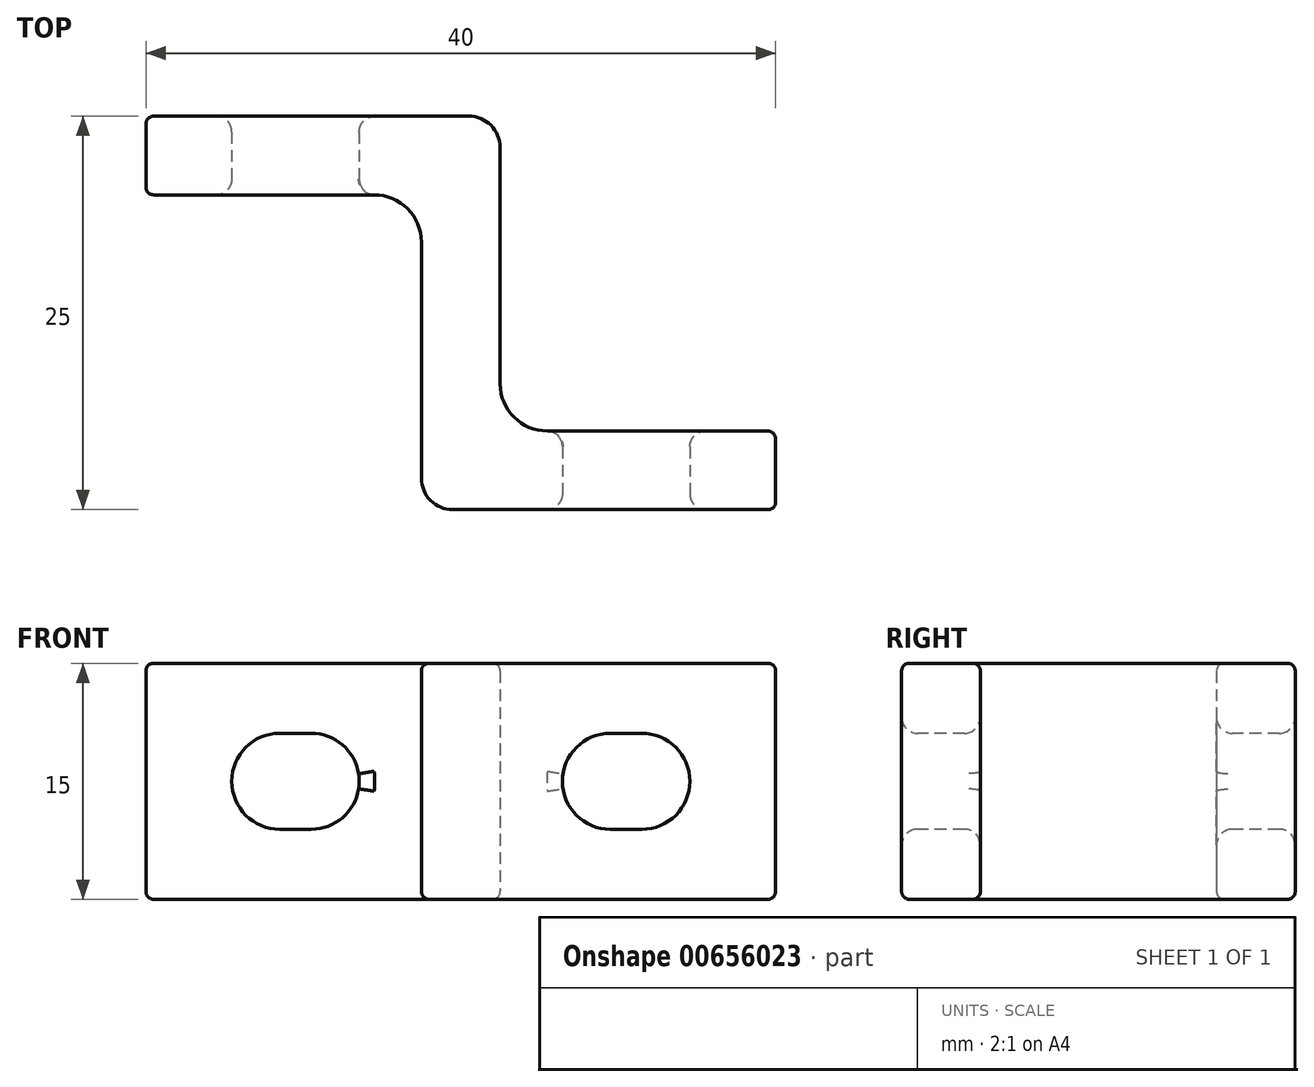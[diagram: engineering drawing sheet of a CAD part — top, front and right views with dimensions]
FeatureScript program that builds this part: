
annotation { "Feature Type Name" : "Feature", "Feature Type Description" : "" }
export const myFeature = defineFeature(function(context is Context, id is Id, definition is map)
    precondition{}
    {
        {
            var Q0;
            Q0=qCreatedBy(makeId("Top.planeOp"),FACE);
            var sketch = newSketch(context, id + "F0", { "sketchPlane" : qUnion([Q0])});
            skLineSegment(sketch, "E0", {"start": v(0, 0) * mm, "end": v(22.5, 0) * mm});
            skLineSegment(sketch, "E1", {"start": v(22.5, 0) * mm, "end": v(22.5, -20) * mm});
            skLineSegment(sketch, "E2", {"start": v(22.5, -20) * mm, "end": v(40, -20) * mm});
            skLineSegment(sketch, "E3", {"start": v(40, -20) * mm, "end": v(40, -25) * mm});
            skLineSegment(sketch, "E4", {"start": v(40, -25) * mm, "end": v(17.5, -25) * mm});
            skLineSegment(sketch, "E5", {"start": v(17.5, -25) * mm, "end": v(17.5, -5) * mm});
            skLineSegment(sketch, "E6", {"start": v(17.5, -5) * mm, "end": v(0, -5) * mm});
            skLineSegment(sketch, "E7", {"start": v(0, -5) * mm, "end": v(0, 0) * mm});
            skSolve(sketch);
        }
        {
            var Q0;
            Q0=makeQuery(id+"F0.imprint","IMPRINT",FACE,{"disambiguationData":[TD([[makeQuery(id+"F0.imprint","IMPRINT",EDGE,{"derivedFrom":sQuery(id+"F0.wireOp",EDGE,"E0")}),-1.0]])]});
            extrude(context, id + "F1", {"entities" : qUnion([Q0]), "depth" : 15 * mm, "offsetDistance" : 25 * mm});
        }
        {
            var Q0;
            Q0=makeQuery(id+"F1.opExtrude","SWEPT_FACE",FACE,{"disambiguationData":[OSD([sQuery(id+"F0.wireOp",EDGE,"E2")])]});
            var sketch = newSketch(context, id + "F2", { "sketchPlane" : qUnion([Q0])});
            skLineSegment(sketch, "E8.bottom", {"start": v(-29.5, 10.55) * mm, "end": v(-31.5, 10.55) * mm});
            skLineSegment(sketch, "E8.top", {"start": v(-29.5, 4.45) * mm, "end": v(-31.5, 4.45) * mm});
            skLineSegment(sketch, "E8.left", {"start": v(-29.5, 10.55) * mm, "end": v(-29.5, 4.45) * mm});
            skLineSegment(sketch, "E8.right", {"start": v(-31.5, 10.55) * mm, "end": v(-31.5, 4.45) * mm});
            skArc(sketch, "E9", {"start": v(-29.5, 4.45) * mm, "mid": v(-26.45, 7.5) * mm, "end": v(-29.5, 10.55) * mm});
            skArc(sketch, "E10", {"start": v(-31.5, 10.55) * mm, "mid": v(-34.55, 7.5) * mm, "end": v(-31.5, 4.45) * mm});
            skLineSegment(sketch, "E11", {"start": v(-20, 25.36) * mm, "end": v(-20, -9.38) * mm, "construction": true});
            skArc(sketch, "E12.MirrorCS", {"start": v(-10.5, 4.45) * mm, "mid": v(-13.55, 7.5) * mm, "end": v(-10.5, 10.55) * mm});
            skLineSegment(sketch, "E13.MirrorCS", {"start": v(-10.5, 10.55) * mm, "end": v(-10.5, 4.45) * mm});
            skLineSegment(sketch, "E14.MirrorCS", {"start": v(-10.5, 10.55) * mm, "end": v(-8.5, 10.55) * mm});
            skLineSegment(sketch, "E15.MirrorCS", {"start": v(-8.5, 10.55) * mm, "end": v(-8.5, 4.45) * mm});
            skArc(sketch, "E16.MirrorCS", {"start": v(-8.5, 10.55) * mm, "mid": v(-5.45, 7.5) * mm, "end": v(-8.5, 4.45) * mm});
            skLineSegment(sketch, "E17.MirrorCS", {"start": v(-10.5, 4.45) * mm, "end": v(-8.5, 4.45) * mm});
            skSolve(sketch);
        }
        {
            var Q0;
            Q0 = qSketchRegion(id + "F2", true);
            extrude(context, id + "F3", {"entities" : qUnion([Q0]), "operationType" : NewBodyOperationType.REMOVE, "endBound" : BoundingType.THROUGH_ALL, "depth" : 25 * mm, "offsetDistance" : 25 * mm, "hasSecondDirection" : true, "secondDirectionBound" : SecondDirectionBoundingType.THROUGH_ALL, "secondDirectionOppositeDirection" : true, "secondDirectionDepth" : 25 * mm});
        }
        {
            var Q0;
            Q0=makeQuery(id+"F1.opExtrude","SWEPT_EDGE",EDGE,{"disambiguationData":[OSD([sQuery(id+"F0.wireOp",EDGE,"E1"),sQuery(id+"F0.wireOp",EDGE,"E2")])]});
            fillet(context, id + "F4", {"entities" : qUnion([Q0]), "radius" : 3 * mm, "tangentPropagation" : true, "allowEdgeOverflow" : false});
        }
        {
            var Q0;
            Q0=makeQuery(id+"F1.opExtrude","SWEPT_EDGE",EDGE,{"disambiguationData":[OSD([sQuery(id+"F0.wireOp",EDGE,"E5"),sQuery(id+"F0.wireOp",EDGE,"E6")])]});
            fillet(context, id + "F5", {"entities" : qUnion([Q0]), "radius" : 3 * mm, "tangentPropagation" : true, "allowEdgeOverflow" : false});
        }
        {
            var Q0;
            Q0=makeQuery(id+"F1.opExtrude","SWEPT_EDGE",EDGE,{"disambiguationData":[OSD([sQuery(id+"F0.wireOp",EDGE,"E0"),sQuery(id+"F0.wireOp",EDGE,"E1")])]});
            fillet(context, id + "F6", {"entities" : qUnion([Q0]), "radius" : 2 * mm, "tangentPropagation" : true, "allowEdgeOverflow" : false});
        }
        {
            var Q0;
            Q0=makeQuery(id+"F1.opExtrude","SWEPT_EDGE",EDGE,{"disambiguationData":[OSD([sQuery(id+"F0.wireOp",EDGE,"E4"),sQuery(id+"F0.wireOp",EDGE,"E5")])]});
            fillet(context, id + "F7", {"entities" : qUnion([Q0]), "radius" : 2 * mm, "tangentPropagation" : true, "allowEdgeOverflow" : false});
        }
        {
            var Q0;
            Q0=makeQuery(id+"F3.boolean.opBoolean","INTERSECT",EDGE,{"derivedFrom":[makeQuery(id+"F1.opExtrude","SWEPT_FACE",FACE,{"disambiguationData":[OSD([sQuery(id+"F0.wireOp",EDGE,"E0")])]}),makeQuery(id+"F3.opExtrude","SWEPT_FACE",FACE,{"disambiguationData":[OSD([sQuery(id+"F2.wireOp",EDGE,"E16.MirrorCS")])]})]});
            fillet(context, id + "F8", {"entities" : qUnion([Q0]), "radius" : 1 * mm, "tangentPropagation" : true, "allowEdgeOverflow" : false});
        }
        {
            var Q0;
            Q0=makeQuery(id+"F3.boolean.opBoolean","INTERSECT",EDGE,{"derivedFrom":[makeQuery(id+"F1.opExtrude","SWEPT_FACE",FACE,{"disambiguationData":[OSD([sQuery(id+"F0.wireOp",EDGE,"E2")])]}),makeQuery(id+"F3.opExtrude","SWEPT_FACE",FACE,{"disambiguationData":[OSD([sQuery(id+"F2.wireOp",EDGE,"E10")])]})]});
            fillet(context, id + "F9", {"entities" : qUnion([Q0]), "radius" : 1 * mm, "tangentPropagation" : true, "allowEdgeOverflow" : false});
        }
        {
            var Q0;
            Q0=makeQuery(id+"F3.boolean.opBoolean","INTERSECT",EDGE,{"derivedFrom":[makeQuery(id+"F1.opExtrude","SWEPT_FACE",FACE,{"disambiguationData":[OSD([sQuery(id+"F0.wireOp",EDGE,"E6")])]}),makeQuery(id+"F3.opExtrude","SWEPT_FACE",FACE,{"disambiguationData":[OSD([sQuery(id+"F2.wireOp",EDGE,"E16.MirrorCS")])]})]});
            fillet(context, id + "F10", {"entities" : qUnion([Q0]), "radius" : 1 * mm, "tangentPropagation" : true, "allowEdgeOverflow" : false});
        }
        {
            var Q0;
            Q0=makeQuery(id+"F3.boolean.opBoolean","INTERSECT",EDGE,{"derivedFrom":[makeQuery(id+"F1.opExtrude","SWEPT_FACE",FACE,{"disambiguationData":[OSD([sQuery(id+"F0.wireOp",EDGE,"E4")])]}),makeQuery(id+"F3.opExtrude","SWEPT_FACE",FACE,{"disambiguationData":[OSD([sQuery(id+"F2.wireOp",EDGE,"E9")])]})]});
            fillet(context, id + "F11", {"entities" : qUnion([Q0]), "radius" : 1 * mm, "tangentPropagation" : true, "allowEdgeOverflow" : false});
        }
        {
            var Q0;
            Q0=makeQuery(id+"F1.opExtrude","CAP_EDGE",EDGE,{"disambiguationData":[OSD([sQuery(id+"F0.wireOp",EDGE,"E0")])],"isStart":false});
            fillet(context, id + "F12", {"entities" : qUnion([Q0]), "radius" : 0.5 * mm, "tangentPropagation" : true, "allowEdgeOverflow" : false});
        }
        {
            var Q0;
            Q0=makeQuery(id+"F1.opExtrude","CAP_EDGE",EDGE,{"disambiguationData":[OSD([sQuery(id+"F0.wireOp",EDGE,"E5")])],"isStart":false});
            fillet(context, id + "F13", {"entities" : qUnion([Q0]), "radius" : 0.5 * mm, "tangentPropagation" : true, "allowEdgeOverflow" : false});
        }
        {
            var Q0;
            Q0=makeQuery(id+"F1.opExtrude","CAP_EDGE",EDGE,{"disambiguationData":[OSD([sQuery(id+"F0.wireOp",EDGE,"E0")])],"isStart":true});
            fillet(context, id + "F14", {"entities" : qUnion([Q0]), "radius" : 0.5 * mm, "tangentPropagation" : true, "allowEdgeOverflow" : false});
        }
        {
            var Q0;
            Q0=makeQuery(id+"F1.opExtrude","CAP_EDGE",EDGE,{"disambiguationData":[OSD([sQuery(id+"F0.wireOp",EDGE,"E5")])],"isStart":true});
            var Q1;
            Q1=makeQuery(id+"F1.opExtrude","SWEPT_EDGE",EDGE,{"disambiguationData":[OSD([sQuery(id+"F0.wireOp",EDGE,"E0"),sQuery(id+"F0.wireOp",EDGE,"E7")])]});
            var Q2;
            Q2=makeQuery(id+"F1.opExtrude","SWEPT_EDGE",EDGE,{"disambiguationData":[OSD([sQuery(id+"F0.wireOp",EDGE,"E2"),sQuery(id+"F0.wireOp",EDGE,"E3")])]});
            fillet(context, id + "F15", {"entities" : qUnion([Q0, Q1, Q2]), "radius" : 0.5 * mm, "tangentPropagation" : true, "allowEdgeOverflow" : false});
        }
    });
